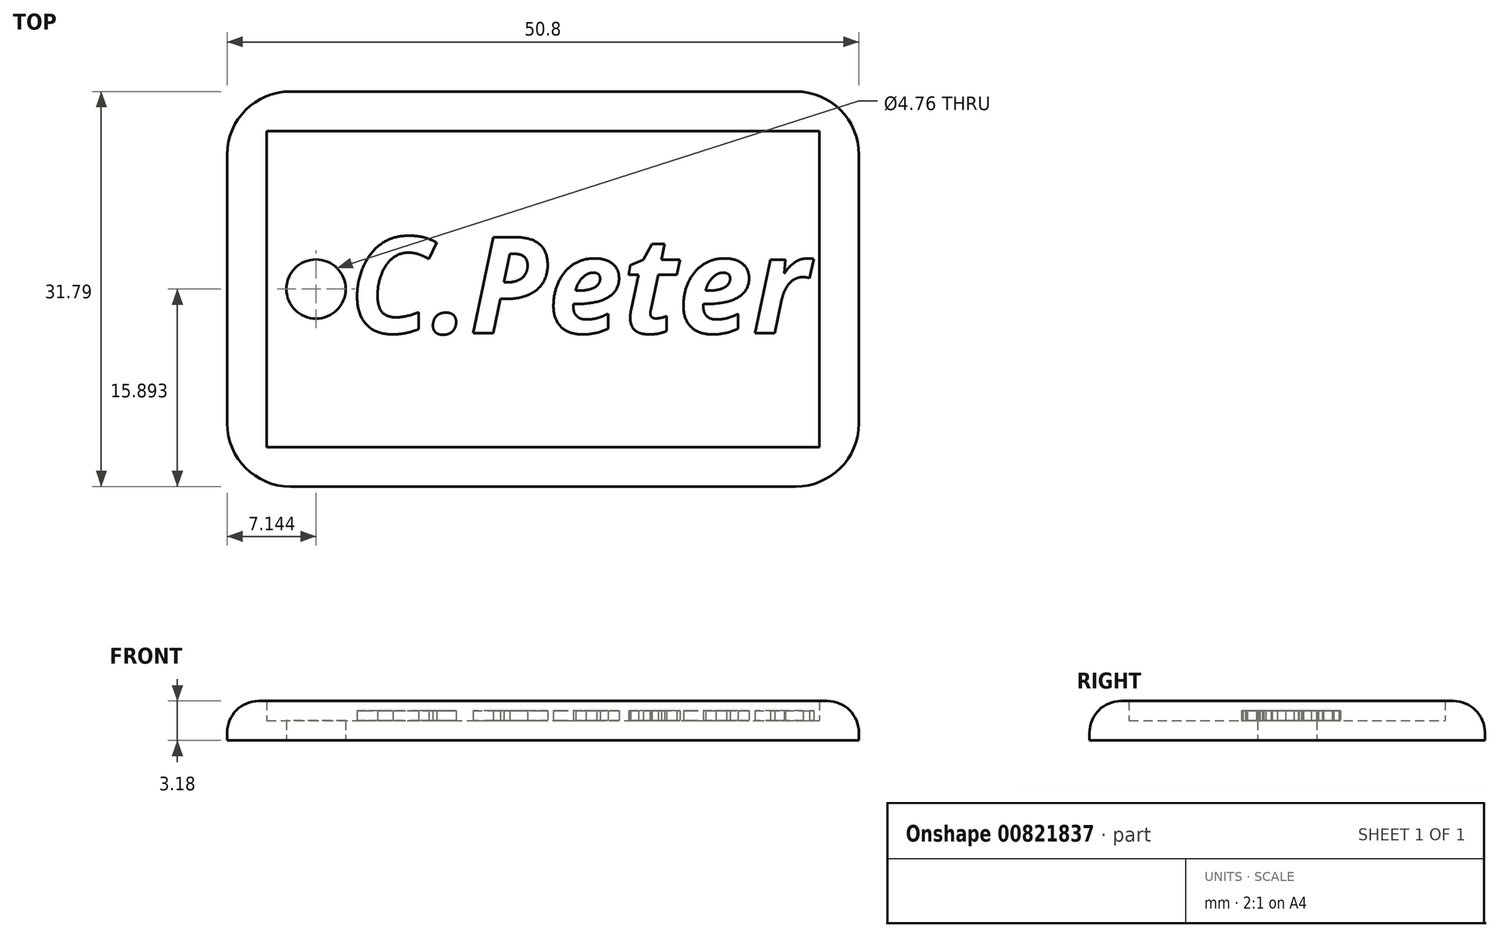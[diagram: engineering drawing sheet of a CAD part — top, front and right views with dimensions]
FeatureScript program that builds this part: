
annotation { "Feature Type Name" : "Feature", "Feature Type Description" : "" }
export const myFeature = defineFeature(function(context is Context, id is Id, definition is map)
    precondition{}
    {
        {
            var Q0;
            Q0=qCreatedBy(makeId("Top.planeOp"),FACE);
            var sketch = newSketch(context, id + "F0", { "sketchPlane" : qUnion([Q0])});
            skLineSegment(sketch, "E0.bottom", {"start": v(0, 0) * mm, "end": v(50.8, 0) * mm});
            skLineSegment(sketch, "E0.top", {"start": v(0, 31.79) * mm, "end": v(50.8, 31.79) * mm});
            skLineSegment(sketch, "E0.left", {"start": v(0, 0) * mm, "end": v(0, 31.79) * mm});
            skLineSegment(sketch, "E0.right", {"start": v(50.8, 0) * mm, "end": v(50.8, 31.79) * mm});
            skCircle(sketch, "E1", {"center": v(7.14, 15.9) * mm, "radius": 2.38 * mm});
            skPoint(sketch, "E1.centerSnap0", {"position": v(0, 15.9) * mm});
            skLineSegment(sketch, "E2.0", {"start": v(3.18, 28.61) * mm, "end": v(47.62, 28.61) * mm});
            skLineSegment(sketch, "E2.1", {"start": v(3.18, 3.18) * mm, "end": v(3.17, 28.61) * mm});
            skLineSegment(sketch, "E2.2", {"start": v(3.18, 3.18) * mm, "end": v(47.62, 3.18) * mm});
            skLineSegment(sketch, "E2.3", {"start": v(47.62, 3.18) * mm, "end": v(47.62, 28.61) * mm});
            skSolve(sketch);
        }
        {
            var Q0;
            Q0=makeQuery(id+"F0.imprint","IMPRINT",FACE,{"disambiguationData":[TD([[makeQuery(id+"F0.imprint","IMPRINT",EDGE,{"derivedFrom":sQuery(id+"F0.wireOp",EDGE,"E1")}),-1.0]])]});
            extrude(context, id + "F1", {"entities" : qUnion([Q0]), "depth" : 1.59 * mm, "offsetDistance" : 25.4 * mm});
        }
        {
            var Q0;
            Q0 = qSketchRegion(id + "F0", true);
            extrude(context, id + "F2", {"entities" : qUnion([Q0]), "operationType" : NewBodyOperationType.ADD, "depth" : 3.17 * mm, "offsetDistance" : 25.4 * mm});
        }
        {
            var Q0;
            Q0=makeQuery(id+"F2.opExtrude","SWEPT_EDGE",EDGE,{"disambiguationData":[OSD([sQuery(id+"F0.wireOp",EDGE,"E0.bottom"),sQuery(id+"F0.wireOp",EDGE,"E0.right")])]});
            var Q1;
            Q1=makeQuery(id+"F2.opExtrude","SWEPT_EDGE",EDGE,{"disambiguationData":[OSD([sQuery(id+"F0.wireOp",EDGE,"E0.top"),sQuery(id+"F0.wireOp",EDGE,"E0.right")])]});
            var Q2;
            Q2=makeQuery(id+"F2.opExtrude","SWEPT_EDGE",EDGE,{"disambiguationData":[OSD([sQuery(id+"F0.wireOp",EDGE,"E0.bottom"),sQuery(id+"F0.wireOp",EDGE,"E0.left")])]});
            var Q3;
            Q3=makeQuery(id+"F2.opExtrude","SWEPT_EDGE",EDGE,{"disambiguationData":[OSD([sQuery(id+"F0.wireOp",EDGE,"E0.top"),sQuery(id+"F0.wireOp",EDGE,"E0.left")])]});
            fillet(context, id + "F3", {"entities" : qUnion([Q0, Q1, Q2, Q3]), "radius" : 5.08 * mm, "tangentPropagation" : true, "allowEdgeOverflow" : false});
        }
        {
            var Q0;
            Q0=makeQuery(id+"F2.opExtrude","CAP_EDGE",EDGE,{"disambiguationData":[OSD([sQuery(id+"F0.wireOp",EDGE,"E0.top")])],"isStart":false});
            var Q1;
            Q1=makeQuery(id+"F2.opExtrude","CAP_EDGE",EDGE,{"disambiguationData":[OSD([sQuery(id+"F0.wireOp",EDGE,"E0.right")])],"isStart":false});
            fillet(context, id + "F4", {"entities" : qUnion([Q0, Q1]), "radius" : 2.54 * mm, "tangentPropagation" : true, "allowEdgeOverflow" : false});
        }
        {
            var Q0;
            Q0=makeQuery(id+"F1.opExtrude","CAP_FACE",FACE,{"disambiguationData":[OSD([sQuery(id+"F0.wireOp",EDGE,"E1"),sQuery(id+"F0.wireOp",EDGE,"E2.0"),sQuery(id+"F0.wireOp",EDGE,"E2.1"),sQuery(id+"F0.wireOp",EDGE,"E2.2"),sQuery(id+"F0.wireOp",EDGE,"E2.3")])],"isStart":false});
            var sketch = newSketch(context, id + "F5", { "sketchPlane" : qUnion([Q0])});
            skText(sketch, "E3", { "text": "C.Peter", "fontName": "OpenSans-BoldItalic.ttf"});
            const initialGuessF5  = {"E3": [0.0098, 0.01235, 1, 0, 0.00778]};
            skSetInitialGuess(sketch, initialGuessF5);
            skSolve(sketch);
        }
        {
            var Q0;
            Q0 = qSketchRegion(id + "F5", true);
            extrude(context, id + "F6", {"entities" : qUnion([Q0]), "operationType" : NewBodyOperationType.ADD, "depth" : 0.8 * mm, "offsetDistance" : 25.4 * mm});
        }
    });
